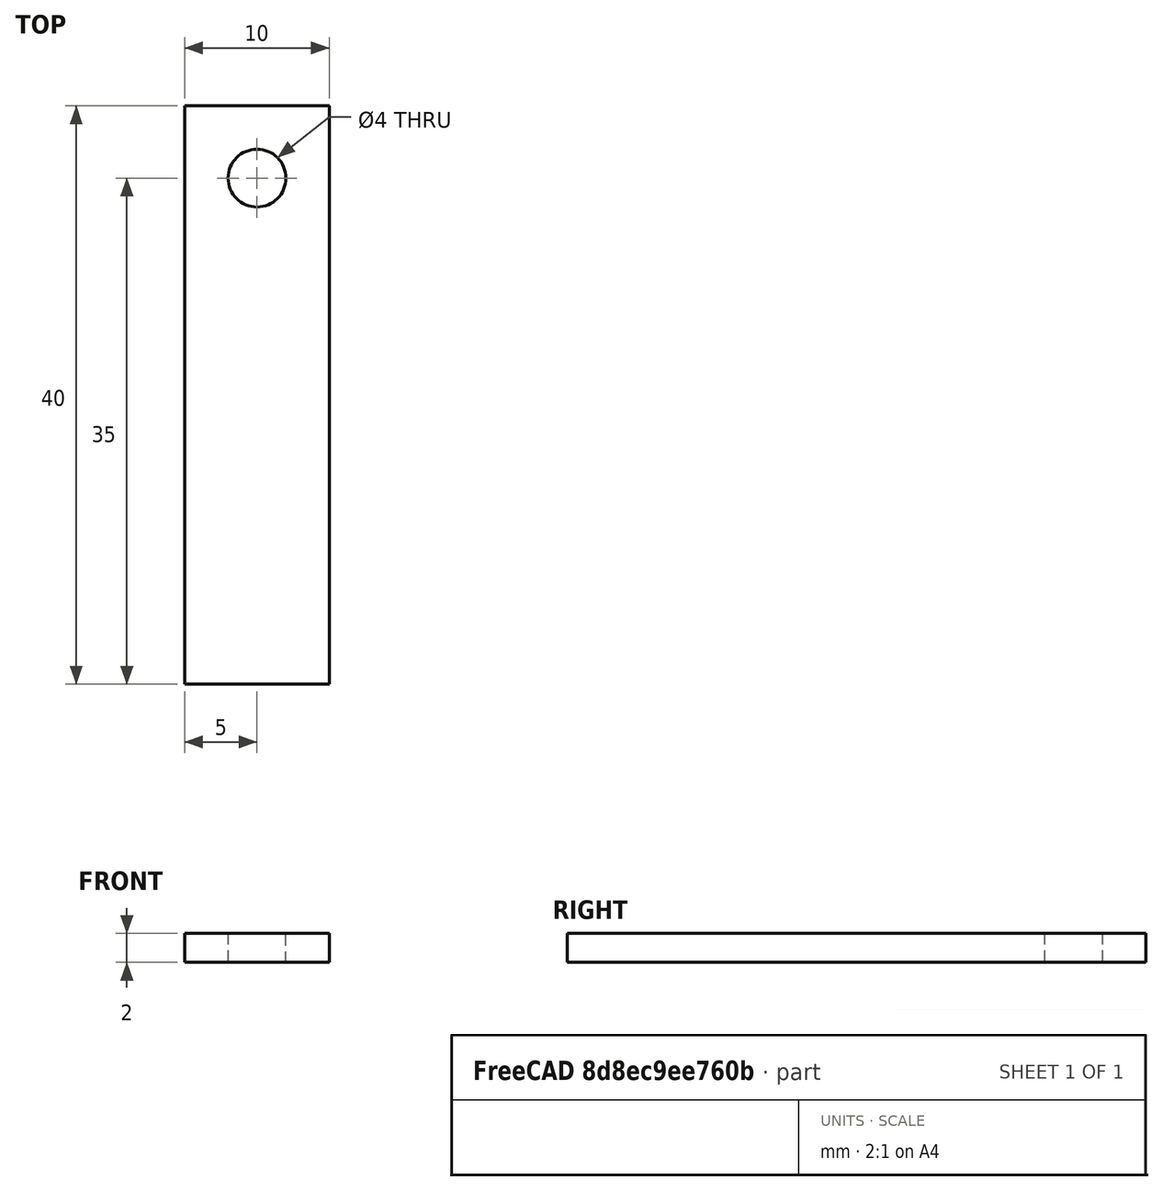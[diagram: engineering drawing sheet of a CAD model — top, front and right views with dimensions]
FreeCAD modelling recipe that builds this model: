
FCSTD DOCUMENT  (FreeCAD 0.18R16146 (Git))
Label: test-strips
License: All rights reserved
LicenseURL: http://en.wikipedia.org/wiki/All_rights_reserved
objects: Sketcher::SketchObject×1, PartDesign::Pad×1, PartDesign::Body×1
note: 4 computed .brp shape members not serialized (recipe doc carries the construction recipe); baked Part::Feature solids carry a one-line shape summary decoded from their .brp

FEATURE [Sketcher::SketchObject] Sketch  label="stip with hole"
  MapMode = 5
  Support = -> [XY_Plane]
  sketch-geometry (5):
    g0: LineSegment StartX=0 StartY=0 StartZ=0 EndX=0 EndY=40 EndZ=0
    g1: LineSegment StartX=0 StartY=40 StartZ=0 EndX=10 EndY=40 EndZ=0
    g2: LineSegment StartX=10 StartY=40 StartZ=0 EndX=10 EndY=0 EndZ=0
    g3: LineSegment StartX=10 StartY=0 StartZ=0 EndX=0 EndY=0 EndZ=0
    g4: Circle CenterX=5 CenterY=35 CenterZ=0 NormalX=0 NormalY=0 NormalZ=1 AngleXU=0 Radius=2
  constraints (14):
    c: Coincident(g0,g1)
    c: Coincident(g1,g2)
    c: Coincident(g2,g3)
    c: Coincident(g3,g0)
    c: Vertical(g0)
    c: Vertical(g2)
    c: Horizontal(g3)
    c: Horizontal(g1)
    c: Distance(g3) = 10
    c: DistanceY(g2,g2) = 40
    c: DistanceX(g0,g4) = 5
    c: DistanceY(g4,g1) = 5
    c: Radius(g4) = 2
    c: Coincident(g0,g-1)
FEATURE [PartDesign::Pad] Pad
  Length = 2
  Length2 = 100
  Profile = -> Sketch
  Type = 0
FEATURE [PartDesign::Body] Body
  Group = -> [Sketch,Pad]
  Origin = -> Origin
  Tip = -> Pad
